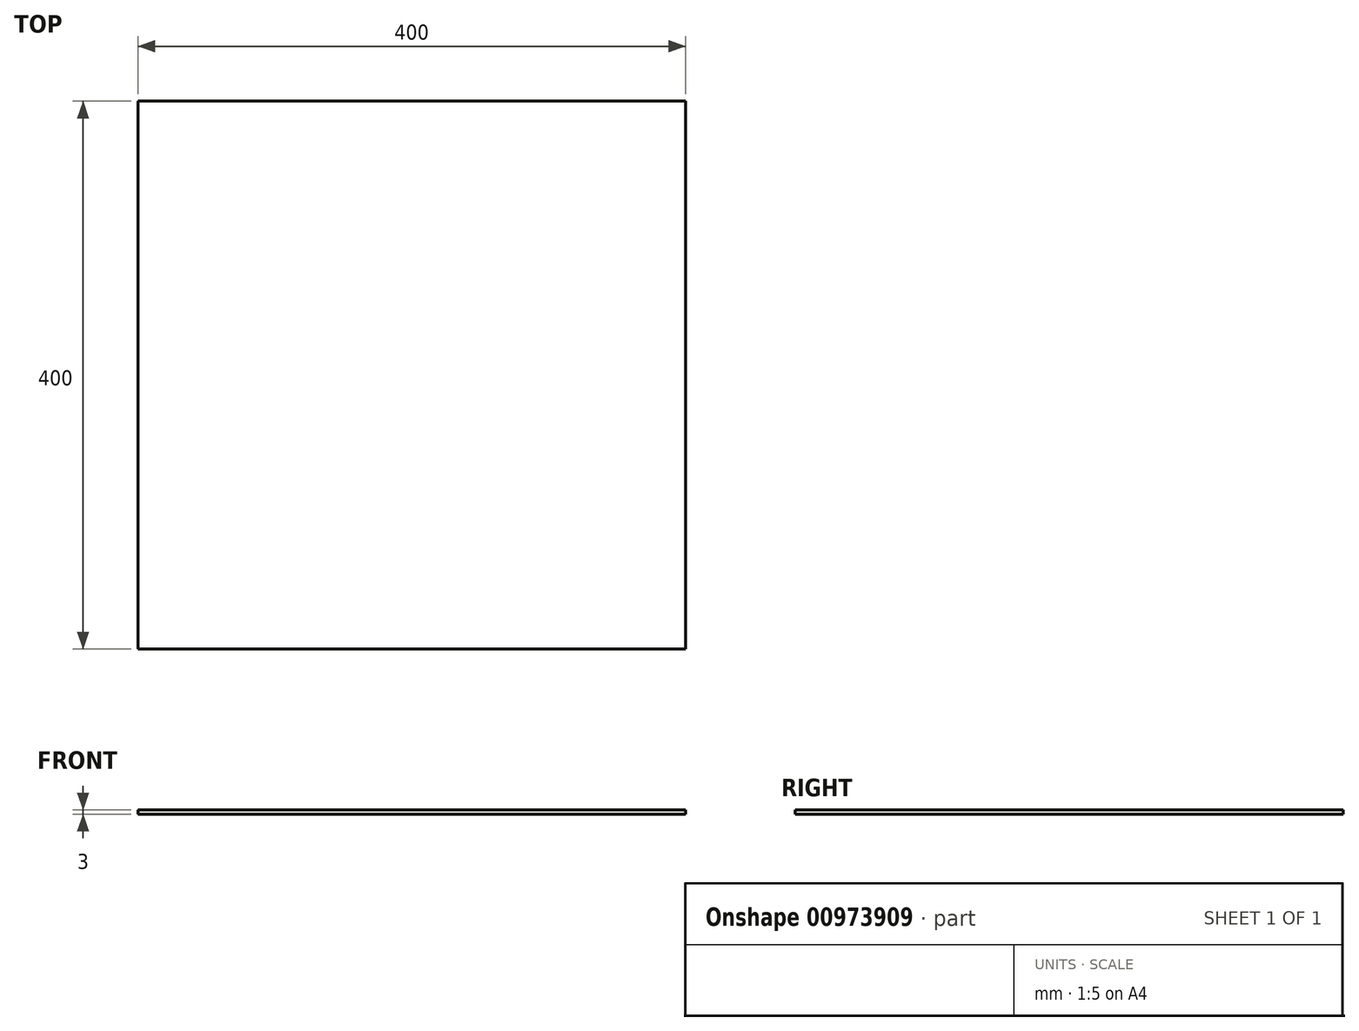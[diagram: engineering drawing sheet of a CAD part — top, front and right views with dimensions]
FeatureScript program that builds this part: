
annotation { "Feature Type Name" : "Feature", "Feature Type Description" : "" }
export const myFeature = defineFeature(function(context is Context, id is Id, definition is map)
    precondition{}
    {
        {
            var Q0;
            Q0=qCreatedBy(makeId("Top.planeOp"),FACE);
            var sketch = newSketch(context, id + "F0", { "sketchPlane" : qUnion([Q0])});
            skLineSegment(sketch, "E0.bottom", {"start": v(200, -200) * mm, "end": v(-200, -200) * mm});
            skLineSegment(sketch, "E0.top", {"start": v(200, 200) * mm, "end": v(-200, 200) * mm});
            skLineSegment(sketch, "E0.left", {"start": v(200, -200) * mm, "end": v(200, 200) * mm});
            skLineSegment(sketch, "E0.right", {"start": v(-200, -200) * mm, "end": v(-200, 200) * mm});
            skPoint(sketch, "E0.middle", {"position": v(0, 0) * mm});
            skSolve(sketch);
        }
        {
            var Q0;
            Q0 = qSketchRegion(id + "F0", true);
            extrude(context, id + "F1", {"entities" : qUnion([Q0]), "depth" : 3 * mm, "offsetDistance" : 25 * mm});
        }
    });
